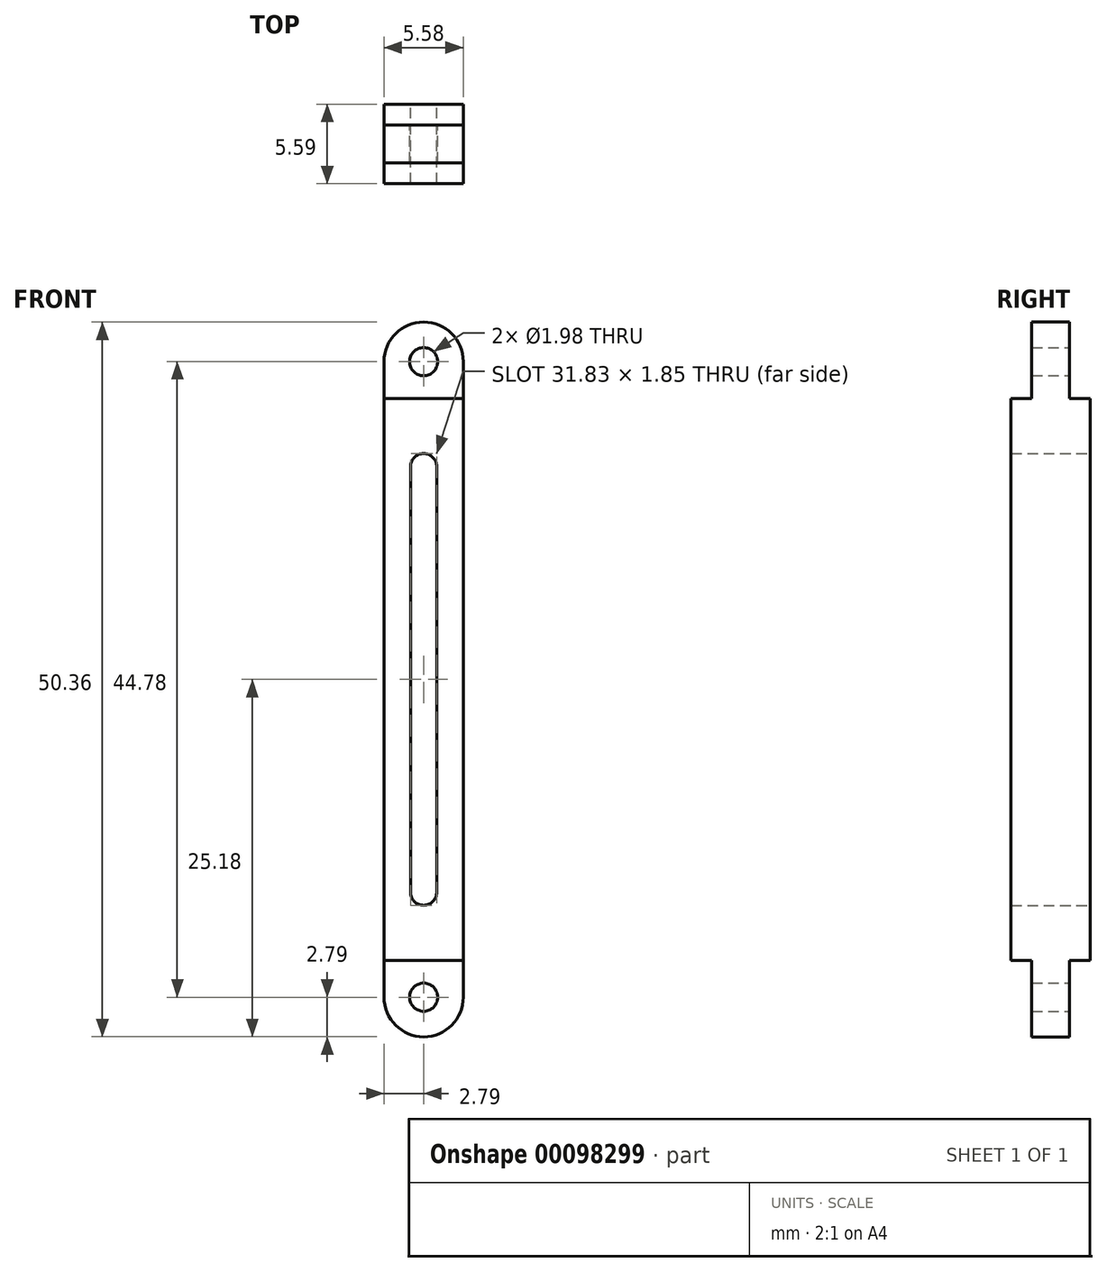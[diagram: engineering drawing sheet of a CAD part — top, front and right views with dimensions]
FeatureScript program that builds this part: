
annotation { "Feature Type Name" : "Feature", "Feature Type Description" : "" }
export const myFeature = defineFeature(function(context is Context, id is Id, definition is map)
    precondition{}
    {
        {
            var Q0;
            Q0=qCreatedBy(makeId("Front.planeOp"),FACE);
            var sketch = newSketch(context, id + "F0", { "sketchPlane" : qUnion([Q0])});
            skLineSegment(sketch, "E0.bottom", {"start": v(2.8, 16.8) * mm, "end": v(-2.8, 16.8) * mm});
            skLineSegment(sketch, "E0.top", {"start": v(2.8, -16.8) * mm, "end": v(-2.8, -16.8) * mm});
            skLineSegment(sketch, "E0.left", {"start": v(2.8, 16.8) * mm, "end": v(2.8, -16.8) * mm});
            skLineSegment(sketch, "E0.right", {"start": v(-2.8, 16.8) * mm, "end": v(-2.8, -16.8) * mm});
            skPoint(sketch, "E0.middle", {"position": v(0, 0) * mm});
            skLineSegment(sketch, "E1.bottom", {"start": v(0.93, 14.99) * mm, "end": v(-0.93, 14.99) * mm});
            skLineSegment(sketch, "E1.top", {"start": v(0.93, -14.99) * mm, "end": v(-0.93, -14.99) * mm});
            skLineSegment(sketch, "E1.left", {"start": v(0.93, 14.99) * mm, "end": v(0.93, -14.99) * mm});
            skLineSegment(sketch, "E1.right", {"start": v(-0.93, 14.99) * mm, "end": v(-0.93, -14.99) * mm});
            skArc(sketch, "E2", {"start": v(0.93, 14.99) * mm, "mid": v(0, 15.91) * mm, "end": v(-0.93, 14.99) * mm});
            skArc(sketch, "E3", {"start": v(-0.93, -14.99) * mm, "mid": v(0, -15.91) * mm, "end": v(0.93, -14.99) * mm});
            skLineSegment(sketch, "E4", {"start": v(-2.8, 16.8) * mm, "end": v(-2.8, 22.4) * mm});
            skLineSegment(sketch, "E5", {"start": v(2.8, 16.8) * mm, "end": v(2.8, 22.4) * mm});
            skArc(sketch, "E6", {"start": v(2.8, 22.4) * mm, "mid": v(0, 25.18) * mm, "end": v(-2.8, 22.4) * mm});
            skLineSegment(sketch, "E7", {"start": v(-2.8, -16.8) * mm, "end": v(-2.8, -22.4) * mm});
            skLineSegment(sketch, "E8", {"start": v(2.8, -16.8) * mm, "end": v(2.8, -22.4) * mm});
            skArc(sketch, "E9", {"start": v(-2.8, -22.4) * mm, "mid": v(0, -25.18) * mm, "end": v(2.8, -22.4) * mm});
            skCircle(sketch, "E10", {"center": v(0, -22.4) * mm, "radius": 1 * mm});
            skCircle(sketch, "E11", {"center": v(0, 22.4) * mm, "radius": 1 * mm});
            skSolve(sketch);
        }
        {
            var Q0;
            Q0=qSketchRegion(id+"F0",true);
            extrude(context, id + "F1", {"entities" : qUnion([Q0]), "depth" : 5.6 * mm});
        }
        {
            var Q0;
            Q0=makeQuery(id+"F1.opExtrude","SWEPT_FACE",FACE,{"disambiguationData":[OSD([sQuery(id+"F0.wireOp",EDGE,"E0.right"),sQuery(id+"F0.wireOp",EDGE,"E4"),sQuery(id+"F0.wireOp",EDGE,"E7")])]});
            var sketch = newSketch(context, id + "F2", { "sketchPlane" : qUnion([Q0])});
            skLineSegment(sketch, "E12", {"start": v(0, 19.8) * mm, "end": v(1.46, 19.8) * mm});
            skLineSegment(sketch, "E13", {"start": v(1.46, 19.8) * mm, "end": v(1.46, 25.18) * mm});
            skLineSegment(sketch, "E14", {"start": v(4.13, 25.18) * mm, "end": v(4.13, 19.8) * mm});
            skLineSegment(sketch, "E15", {"start": v(4.13, 19.8) * mm, "end": v(5.59, 19.8) * mm});
            skLineSegment(sketch, "E16", {"start": v(2.8, 0) * mm, "end": v(2.8, 34.17) * mm, "construction": true});
            skPoint(sketch, "E16.startSnap0", {"position": v(2.8, 22.4) * mm});
            skLineSegment(sketch, "E17.0.0", {"start": v(0, 25.18) * mm, "end": v(0, 22.4) * mm});
            skLineSegment(sketch, "E17.0.2", {"start": v(5.59, 22.4) * mm, "end": v(5.59, 25.18) * mm});
            skLineSegment(sketch, "E18.MirrorCS", {"start": v(0, -19.8) * mm, "end": v(1.46, -19.8) * mm});
            skPoint(sketch, "E19.MirrorP", {"position": v(2.8, -22.4) * mm});
            skLineSegment(sketch, "E20.MirrorCS", {"start": v(4.13, -25.18) * mm, "end": v(4.13, -19.8) * mm});
            skLineSegment(sketch, "E21.MirrorCS", {"start": v(5.59, -22.4) * mm, "end": v(5.59, -25.18) * mm});
            skLineSegment(sketch, "E22.MirrorCS", {"start": v(1.46, -19.8) * mm, "end": v(1.46, -25.18) * mm});
            skLineSegment(sketch, "E23.MirrorCS", {"start": v(0, -25.18) * mm, "end": v(0, -22.4) * mm});
            skLineSegment(sketch, "E24.MirrorCS", {"start": v(4.13, -19.8) * mm, "end": v(5.59, -19.8) * mm});
            skLineSegment(sketch, "E25", {"start": v(1.46, 25.18) * mm, "end": v(0, 25.18) * mm});
            skLineSegment(sketch, "E26", {"start": v(4.13, 25.18) * mm, "end": v(5.59, 25.18) * mm});
            skLineSegment(sketch, "E27", {"start": v(4.13, -25.18) * mm, "end": v(5.59, -25.18) * mm});
            skLineSegment(sketch, "E28", {"start": v(1.46, -25.18) * mm, "end": v(0, -25.18) * mm});
            skLineSegment(sketch, "E29.0.1", {"start": v(1.46, 22.4) * mm, "end": v(4.13, 22.4) * mm});
            skLineSegment(sketch, "E29.0.3", {"start": v(4.13, 22.4) * mm, "end": v(1.46, 22.4) * mm});
            skLineSegment(sketch, "E30", {"start": v(0, 25.18) * mm, "end": v(5.59, 25.18) * mm, "construction": true});
            skPoint(sketch, "E31.orphan", {"position": v(0, 22.4) * mm});
            skPoint(sketch, "E32.orphan", {"position": v(5.59, 22.4) * mm});
            skLineSegment(sketch, "E33", {"start": v(0, 22.4) * mm, "end": v(0, 19.8) * mm});
            skLineSegment(sketch, "E34", {"start": v(5.59, 19.8) * mm, "end": v(5.59, 22.4) * mm});
            skSolve(sketch);
        }
        {
            var Q0;
            {var subQ0=sQuery(id+"F2.wireOp",EDGE,"E12");Q0=makeQuery(id+"F2.imprint","IMPRINT",FACE,{"disambiguationData":[TD([[makeQuery(id+"F2.imprint","IMPRINT",EDGE,{"derivedFrom":subQ0}),1.0]])]});}
            var Q1;
            {var subQ0=sQuery(id+"F2.wireOp",EDGE,"E25");Q1=makeQuery(id+"F2.imprint","IMPRINT",FACE,{"disambiguationData":[TD([[makeQuery(id+"F2.imprint","IMPRINT",EDGE,{"derivedFrom":subQ0}),1.0]])]});}
            var Q2;
            {var subQ0=sQuery(id+"F2.wireOp",EDGE,"E26");Q2=makeQuery(id+"F2.imprint","IMPRINT",FACE,{"disambiguationData":[TD([[makeQuery(id+"F2.imprint","IMPRINT",EDGE,{"derivedFrom":subQ0}),-1.0]])]});}
            var Q3;
            {var subQ0=sQuery(id+"F2.wireOp",EDGE,"E15");Q3=makeQuery(id+"F2.imprint","IMPRINT",FACE,{"disambiguationData":[TD([[makeQuery(id+"F2.imprint","IMPRINT",EDGE,{"derivedFrom":subQ0}),1.0]])]});}
            var Q4;
            {var subQ5=sQuery(id+"F2.wireOp",EDGE,"E23.MirrorCS");Q4=makeQuery(id+"F2.imprint","IMPRINT",FACE,{"disambiguationData":[TD([[makeQuery(id+"F2.imprint","IMPRINT",EDGE,{"derivedFrom":subQ5}),-1.0]])]});}
            var Q5;
            {var subQ0=sQuery(id+"F2.wireOp",EDGE,"E18.MirrorCS");Q5=makeQuery(id+"F2.imprint","IMPRINT",FACE,{"disambiguationData":[TD([[makeQuery(id+"F2.imprint","IMPRINT",EDGE,{"derivedFrom":subQ0}),-1.0]])]});}
            var Q6;
            {var subQ0=sQuery(id+"F2.wireOp",EDGE,"E24.MirrorCS");Q6=makeQuery(id+"F2.imprint","IMPRINT",FACE,{"disambiguationData":[TD([[makeQuery(id+"F2.imprint","IMPRINT",EDGE,{"derivedFrom":subQ0}),-1.0]])]});}
            var Q7;
            {var subQ5=sQuery(id+"F2.wireOp",EDGE,"E21.MirrorCS");Q7=makeQuery(id+"F2.imprint","IMPRINT",FACE,{"disambiguationData":[TD([[makeQuery(id+"F2.imprint","IMPRINT",EDGE,{"derivedFrom":subQ5}),-1.0]])]});}
            extrude(context, id + "F3", {"entities" : qUnion([Q0, Q1, Q2, Q3, Q4, Q5, Q6, Q7]), "operationType" : NewBodyOperationType.REMOVE, "endBound" : BoundingType.THROUGH_ALL, "oppositeDirection" : true, "depth" : 25.4 * mm});
        }
    });
